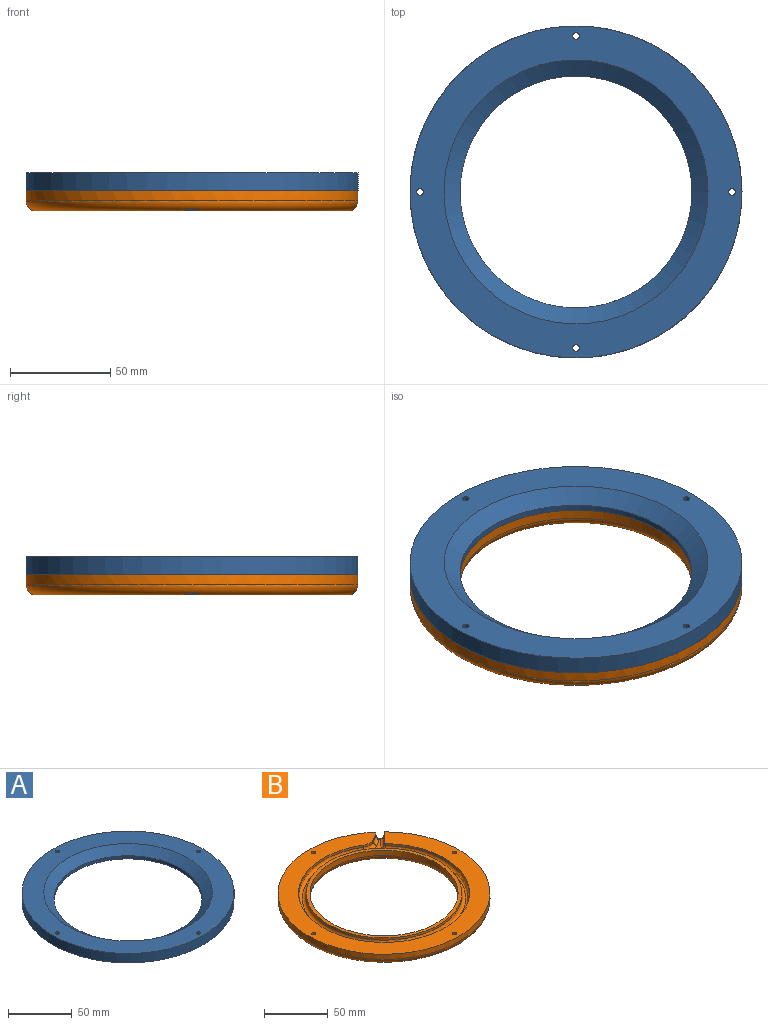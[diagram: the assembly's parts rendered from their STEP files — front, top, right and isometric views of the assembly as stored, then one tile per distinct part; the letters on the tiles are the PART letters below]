
ASSEMBLY  parts=2 mates=1
PART A: 9 faces, bbox 166x166x9 mm
  f0: cylinder r=58mm len=116mm, axis (0,0,1), area 1093.3mm2, adj f1,f4
  f1: plane 166x166mm, normal (0,0,-1), area 11039.9mm2, adj f0,f2,f5,f6,f7,f8
  f2: cylinder r=83mm len=166mm, axis (0,0,1), area 4693.5mm2, adj f1,f3
  f3: plane 166x166mm, normal (0,0,1), area 7923.4mm2, adj f2,f4,f5,f6,f7,f8
  f4: cone r=66mm half-angle=53.1deg, axis (0,0,1), area 3895.6mm2, adj f0,f3
  f5: cylinder r=1.65mm len=9mm, axis (0,0,1), area 93.3mm2, adj f1,f3
  f6: cylinder r=1.65mm len=9mm, axis (0,0,1), area 93.3mm2, adj f1,f3
  f7: cylinder r=1.65mm len=9mm, axis (0,0,1), area 93.3mm2, adj f1,f3
  f8: cylinder r=1.65mm len=9mm, axis (0,0,1), area 93.3mm2, adj f1,f3
PART B: 33 faces, bbox 179.7x179.7x10.1 mm
  f0: cylinder r=83mm len=166mm, axis (0,0,-1), area 2566.6mm2, adj f4,f16,f17,f22,f26,f32
  f1: cylinder r=67mm len=134mm, axis (0,0,-1), area 808mm2, adj f4,f14,f15,f21
  f2: cylinder r=58mm len=116mm, axis (0,0,-1), area 1822.1mm2, adj f7,f31
  f3: plane 155.78x155.78mm, normal (0,0,-1), area 6540mm2, adj f27,f28,f29,f30,f31,f32
  f4: plane 166x166mm, normal (0,0,1), area 7371.9mm2, adj f0,f1,f8,f9,f10,f11,f12,f13
  f5: plane 21.14x14.48mm, normal (0,0,1), area 56.6mm2, adj f18,f19,f20,f23,f24,f25
  f6: cylinder r=61mm len=122mm, axis (0,0,-1), area 766.5mm2, adj f7,f18
  f7: plane 122x122mm, normal (0,0,1), area 1121.5mm2, adj f2,f6
  f8: cylinder r=1.6mm len=7.5mm, axis (0,0,1), area 75.4mm2, adj f4,f27
  f9: cylinder r=1.6mm len=7.5mm, axis (0,0,1), area 75.4mm2, adj f4,f30
  f10: cylinder r=1.6mm len=7.5mm, axis (0,0,1), area 75.4mm2, adj f4,f28
  f11: cylinder r=1.6mm len=7.5mm, axis (0,0,1), area 75.4mm2, adj f4,f29
  f12: plane 9.9x9.9mm, normal (-0.71,0.71,0), area 28mm2, adj f4,f15,f16,f20
  f13: plane 7.88x4.81mm, normal (0.52,-0.85,0), area 18.5mm2, adj f4,f14,f17,f25
  f14: cylinder r=10mm len=10.41mm, axis (0,0,-1), area 21.9mm2, adj f1,f4,f13,f23
  f15: cylinder r=1mm len=2mm, axis (0,0,-1), area 3.1mm2, adj f1,f4,f12,f19
  f16: cylinder r=1mm len=2mm, axis (0,0,-1), area 3.2mm2, adj f0,f4,f12,f22
  f17: cylinder r=1mm len=2mm, axis (0,0,-1), area 3.8mm2, adj f0,f4,f13,f26
  f18: torus R=64mm, axis (0,0,1), area 1838.4mm2, adj f5,f6,f21
  f19: torus R=4mm, axis (0,0,1), area 15.3mm2, adj f5,f15,f20,f21
  f20: cylinder r=3mm len=12.02mm, axis (0.71,0.71,0), area 61.1mm2, adj f5,f12,f19,f22
  f21: torus R=64mm, axis (0,0,1), area 1872.8mm2, adj f1,f18,f19,f23
  f22: bspline ~6x4.99mm, area 15.4mm2, adj f0,f16,f20,f24,f32
  f23: torus R=13mm, axis (0,0,1), area 57.2mm2, adj f5,f14,f21,f25
  f24: torus R=80mm, axis (0,0,1), area 2.1mm2, adj f5,f22,f26,f32
  f25: cylinder r=3mm len=9.45mm, axis (-0.85,-0.52,0), area 41.5mm2, adj f5,f13,f23,f26
  f26: bspline ~6x4.62mm, area 16.1mm2, adj f0,f17,f24,f25,f32
  f27: cone r=1.6mm half-angle=45deg, axis (0,0,-1), area 53.6mm2, adj f3,f8,f32
  f28: cone r=1.6mm half-angle=45deg, axis (0,0,-1), area 63.3mm2, adj f3,f10,f32
  f29: cone r=1.6mm half-angle=45deg, axis (0,0,-1), area 53.6mm2, adj f3,f11,f32
  f30: cone r=1.6mm half-angle=45deg, axis (0,0,-1), area 54.5mm2, adj f3,f9,f32
  f31: torus R=63mm, axis (0,0,-1), area 2951.8mm2, adj f2,f3
  f32: torus R=78mm, axis (0,0,-1), area 3912.6mm2, adj f0,f3,f22,f24,f26,f27,f28,f29
PLACE A t=(20.7,-36.45,-62.6)mm
PLACE B t=(20.7,-36.45,-72.6)mm
MATE fastened A.f8 <-> B.f11  axis (0,0,1) through (20.7,41.55,-62.6)mm
